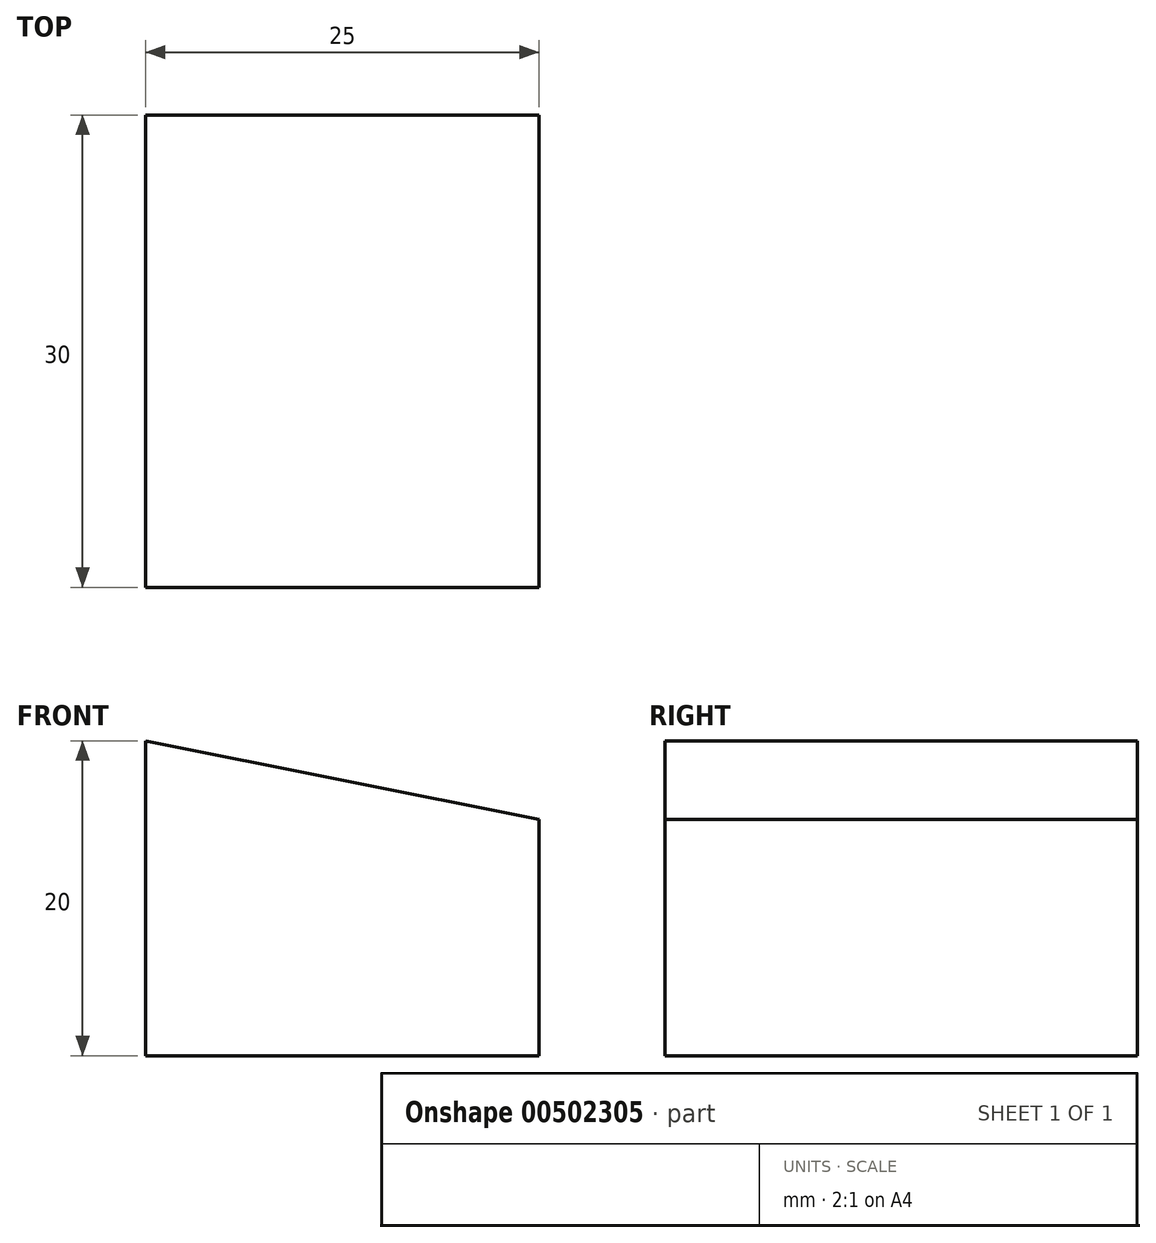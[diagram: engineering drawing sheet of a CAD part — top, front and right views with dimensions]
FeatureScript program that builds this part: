
annotation { "Feature Type Name" : "Feature", "Feature Type Description" : "" }
export const myFeature = defineFeature(function(context is Context, id is Id, definition is map)
    precondition{}
    {
        {
            var Q0;
            Q0=qCreatedBy(makeId("Front.planeOp"),FACE);
            var sketch = newSketch(context, id + "F0", { "sketchPlane" : qUnion([Q0])});
            skLineSegment(sketch, "E0", {"start": v(-23.8, 18.52) * mm, "end": v(-23.8, -1.48) * mm});
            skLineSegment(sketch, "E1", {"start": v(1.2, -1.48) * mm, "end": v(-23.8, -1.48) * mm});
            skLineSegment(sketch, "E2", {"start": v(1.2, -1.48) * mm, "end": v(1.2, 13.52) * mm});
            skLineSegment(sketch, "E3", {"start": v(-23.8, 18.52) * mm, "end": v(1.2, 13.52) * mm});
            skSolve(sketch);
        }
        {
            var Q0;
            Q0 = qSketchRegion(id + "F0", true);
            extrude(context, id + "F1", {"entities" : qUnion([Q0]), "depth" : 30 * mm});
        }
    });
